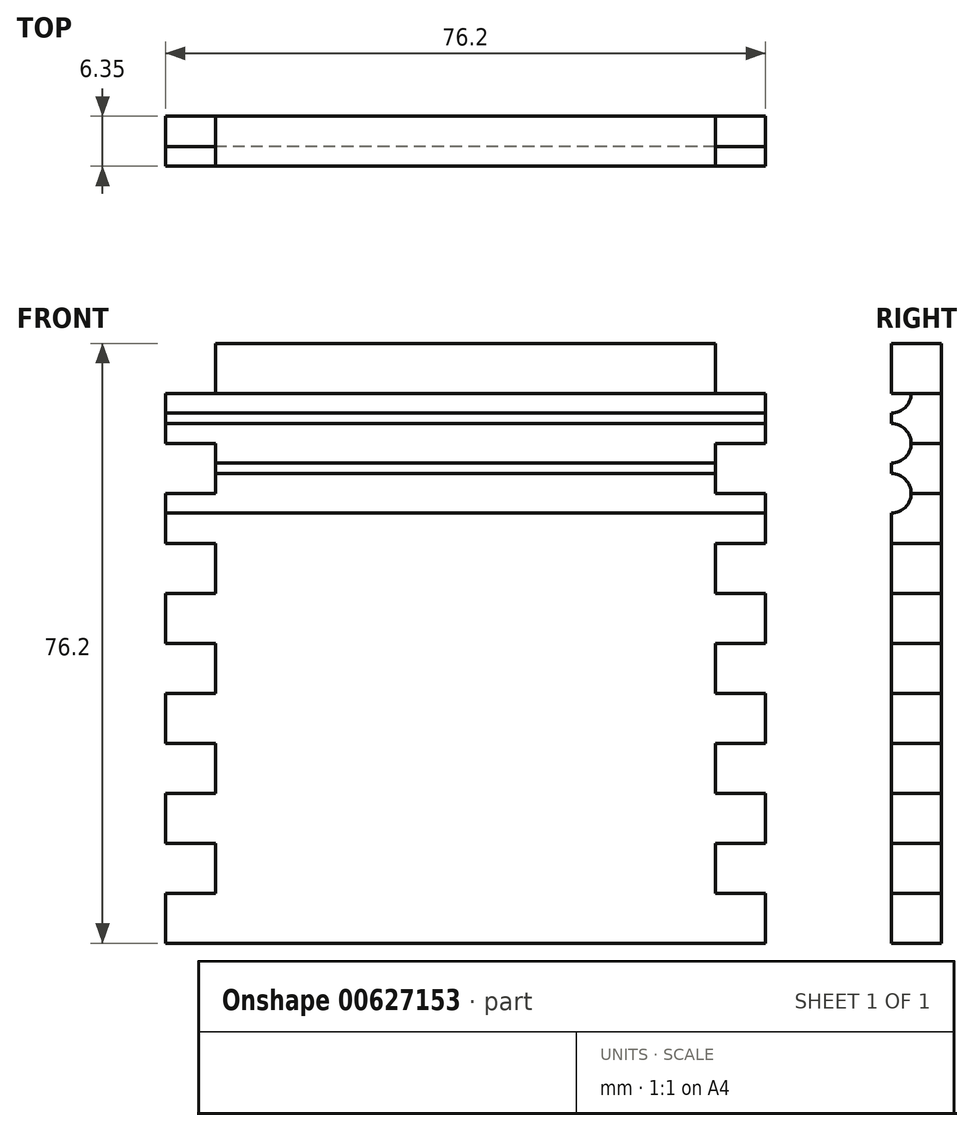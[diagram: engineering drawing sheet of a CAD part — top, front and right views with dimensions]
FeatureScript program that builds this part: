
annotation { "Feature Type Name" : "Feature", "Feature Type Description" : "" }
export const myFeature = defineFeature(function(context is Context, id is Id, definition is map)
    precondition{}
    {
        {
            var Q0;
            Q0=qCreatedBy(makeId("Front.planeOp"),FACE);
            var sketch = newSketch(context, id + "F0", { "sketchPlane" : qUnion([Q0])});
            skLineSegment(sketch, "E0", {"start": v(-134.03, 0) * mm, "end": v(134.03, 0) * mm, "construction": true});
            skLineSegment(sketch, "E1.bottom", {"start": v(-38.1, 38.1) * mm, "end": v(38.1, 38.1) * mm});
            skLineSegment(sketch, "E1.top", {"start": v(-38.1, -38.1) * mm, "end": v(38.1, -38.1) * mm});
            skLineSegment(sketch, "E1.left", {"start": v(-38.1, 38.1) * mm, "end": v(-38.1, -38.1) * mm});
            skLineSegment(sketch, "E1.right", {"start": v(38.1, 38.1) * mm, "end": v(38.1, -38.1) * mm});
            skLineSegment(sketch, "E2", {"start": v(0, 82.06) * mm, "end": v(0, -82.06) * mm, "construction": true});
            skLineSegment(sketch, "E3", {"start": v(-31.75, 38.1) * mm, "end": v(-31.75, -38.1) * mm, "construction": true});
            skLineSegment(sketch, "E4", {"start": v(31.75, 38.1) * mm, "end": v(31.75, -38.1) * mm, "construction": true});
            skLineSegment(sketch, "E5", {"start": v(-38.1, 31.75) * mm, "end": v(-31.75, 31.75) * mm});
            skLineSegment(sketch, "E6.0.1.0", {"start": v(-38.1, 25.4) * mm, "end": v(-31.75, 25.4) * mm});
            skLineSegment(sketch, "E6.0.2.0", {"start": v(-38.1, 19.05) * mm, "end": v(-31.75, 19.05) * mm});
            skLineSegment(sketch, "E6.0.3.0", {"start": v(-38.1, 12.7) * mm, "end": v(-31.75, 12.7) * mm});
            skLineSegment(sketch, "E6.0.4.0", {"start": v(-38.1, 6.35) * mm, "end": v(-31.75, 6.35) * mm});
            skLineSegment(sketch, "E6.0.5.0", {"start": v(-38.1, 0) * mm, "end": v(-31.75, 0) * mm});
            skLineSegment(sketch, "E6.0.6.0", {"start": v(-38.1, -6.35) * mm, "end": v(-31.75, -6.35) * mm});
            skLineSegment(sketch, "E6.0.7.0", {"start": v(-38.1, -12.7) * mm, "end": v(-31.75, -12.7) * mm});
            skLineSegment(sketch, "E6.0.8.0", {"start": v(-38.1, -19.05) * mm, "end": v(-31.75, -19.05) * mm});
            skLineSegment(sketch, "E6.0.9.0", {"start": v(-38.1, -25.4) * mm, "end": v(-31.75, -25.4) * mm});
            skLineSegment(sketch, "E6.0.10.0", {"start": v(-38.1, -31.75) * mm, "end": v(-31.75, -31.75) * mm});
            skLineSegment(sketch, "E6.0.11.0", {"start": v(-38.1, -38.1) * mm, "end": v(-31.75, -38.1) * mm});
            skLineSegment(sketch, "E6.direction1", {"start": v(-38.1, 31.75) * mm, "end": v(-13.1, 31.75) * mm, "construction": true});
            skLineSegment(sketch, "E6.direction2", {"start": v(-38.1, 31.75) * mm, "end": v(-38.1, 25.4) * mm, "construction": true});
            skLineSegment(sketch, "E7", {"start": v(-31.75, 38.1) * mm, "end": v(-31.75, 31.75) * mm});
            skLineSegment(sketch, "E8", {"start": v(-31.75, 25.4) * mm, "end": v(-31.75, 19.05) * mm});
            skLineSegment(sketch, "E9", {"start": v(-31.75, 12.7) * mm, "end": v(-31.75, 6.35) * mm});
            skLineSegment(sketch, "E10", {"start": v(-31.75, 0) * mm, "end": v(-31.75, -6.35) * mm});
            skLineSegment(sketch, "E11", {"start": v(-31.75, -12.7) * mm, "end": v(-31.75, -19.05) * mm});
            skLineSegment(sketch, "E12", {"start": v(-31.75, -25.4) * mm, "end": v(-31.75, -31.75) * mm});
            skLineSegment(sketch, "E13.MirrorCS", {"start": v(31.75, 38.1) * mm, "end": v(31.75, 31.75) * mm});
            skLineSegment(sketch, "E14.MirrorCS", {"start": v(38.1, 31.75) * mm, "end": v(38.1, 25.4) * mm, "construction": true});
            skLineSegment(sketch, "E15.MirrorCS", {"start": v(38.1, 31.75) * mm, "end": v(31.75, 31.75) * mm});
            skLineSegment(sketch, "E16.MirrorCS", {"start": v(38.1, 25.4) * mm, "end": v(31.75, 25.4) * mm});
            skLineSegment(sketch, "E17.MirrorCS", {"start": v(31.75, -25.4) * mm, "end": v(31.75, -31.75) * mm});
            skLineSegment(sketch, "E18.MirrorCS", {"start": v(31.75, 25.4) * mm, "end": v(31.75, 19.05) * mm});
            skLineSegment(sketch, "E19.MirrorCS", {"start": v(31.75, 12.7) * mm, "end": v(31.75, 6.35) * mm});
            skLineSegment(sketch, "E20.MirrorCS", {"start": v(31.75, -12.7) * mm, "end": v(31.75, -19.05) * mm});
            skLineSegment(sketch, "E21.MirrorCS", {"start": v(38.1, -38.1) * mm, "end": v(31.75, -38.1) * mm});
            skLineSegment(sketch, "E22.MirrorCS", {"start": v(31.75, 0) * mm, "end": v(31.75, -6.35) * mm});
            skLineSegment(sketch, "E23.MirrorCS", {"start": v(38.1, -25.4) * mm, "end": v(31.75, -25.4) * mm});
            skLineSegment(sketch, "E24.MirrorCS", {"start": v(38.1, -31.75) * mm, "end": v(31.75, -31.75) * mm});
            skLineSegment(sketch, "E25.MirrorCS", {"start": v(38.1, -19.05) * mm, "end": v(31.75, -19.05) * mm});
            skLineSegment(sketch, "E26.MirrorCS", {"start": v(38.1, 19.05) * mm, "end": v(31.75, 19.05) * mm});
            skLineSegment(sketch, "E27.MirrorCS", {"start": v(38.1, 12.7) * mm, "end": v(31.75, 12.7) * mm});
            skLineSegment(sketch, "E28.MirrorCS", {"start": v(38.1, 0) * mm, "end": v(31.75, 0) * mm});
            skLineSegment(sketch, "E29.MirrorCS", {"start": v(38.1, -6.35) * mm, "end": v(31.75, -6.35) * mm});
            skLineSegment(sketch, "E30.MirrorCS", {"start": v(38.1, -12.7) * mm, "end": v(31.75, -12.7) * mm});
            skLineSegment(sketch, "E31.MirrorCS", {"start": v(38.1, 6.35) * mm, "end": v(31.75, 6.35) * mm});
            skSolve(sketch);
        }
        {
            var Q0;
            Q0=makeQuery(id+"F0.imprint","IMPRINT",FACE,{"disambiguationData":[TD([[makeQuery(id+"F0.imprint","IMPRINT",EDGE,{"derivedFrom":sQuery(id+"F0.wireOp",EDGE,"E1.top")}),1.0]])]});
            extrude(context, id + "F1", {"entities" : qUnion([Q0]), "depth" : 6.35 * mm, "offsetDistance" : 25 * mm});
        }
        {
            var Q0;
            {var subQ0=sQuery(id+"F0.wireOp",EDGE,"E1.left");Q0=makeQuery(id+"F1.opExtrude","SWEPT_FACE",FACE,{"disambiguationData":[OSD([subQ0]),TDD([makeQuery(id+"F0.imprint","IMPRINT",EDGE,{"disambiguationData":[TD([[makeQuery(id+"F0.imprint","INTERSECT",VERTEX,{"derivedFrom":[subQ0,sQuery(id+"F0.wireOp",EDGE,"E5")]}),-1.0]])],"derivedFrom":subQ0})])]});}
            var sketch = newSketch(context, id + "F2", { "sketchPlane" : qUnion([Q0])});
            skLineSegment(sketch, "E32.0.0", {"start": v(0, 38.1) * mm, "end": v(0, 31.75) * mm, "construction": true});
            skLineSegment(sketch, "E32.0.1", {"start": v(0, 31.75) * mm, "end": v(6.35, 31.75) * mm, "construction": true});
            skLineSegment(sketch, "E32.0.2", {"start": v(6.35, 31.75) * mm, "end": v(6.35, 38.1) * mm, "construction": true});
            skLineSegment(sketch, "E32.0.3", {"start": v(6.35, 38.1) * mm, "end": v(0, 38.1) * mm, "construction": true});
            skLineSegment(sketch, "E33", {"start": v(6.35, 38.1) * mm, "end": v(6.35, 5.95) * mm, "construction": true});
            skLineSegment(sketch, "E34.0.0", {"start": v(0, 31.75) * mm, "end": v(0, 25.4) * mm, "construction": true});
            skLineSegment(sketch, "E34.0.1", {"start": v(0, 25.4) * mm, "end": v(6.35, 25.4) * mm, "construction": true});
            skLineSegment(sketch, "E34.0.2", {"start": v(6.35, 25.4) * mm, "end": v(6.35, 31.75) * mm, "construction": true});
            skLineSegment(sketch, "E34.0.3", {"start": v(6.35, 31.75) * mm, "end": v(0, 31.75) * mm, "construction": true});
            skLineSegment(sketch, "E35.0.0", {"start": v(0, 25.4) * mm, "end": v(0, 19.05) * mm, "construction": true});
            skLineSegment(sketch, "E35.0.1", {"start": v(0, 19.05) * mm, "end": v(6.35, 19.05) * mm, "construction": true});
            skLineSegment(sketch, "E35.0.2", {"start": v(6.35, 19.05) * mm, "end": v(6.35, 25.4) * mm, "construction": true});
            skLineSegment(sketch, "E35.0.3", {"start": v(6.35, 25.4) * mm, "end": v(0, 25.4) * mm, "construction": true});
            skLineSegment(sketch, "E36.0.0", {"start": v(0, 19.05) * mm, "end": v(0, 12.7) * mm, "construction": true});
            skLineSegment(sketch, "E36.0.1", {"start": v(0, 12.7) * mm, "end": v(6.35, 12.7) * mm, "construction": true});
            skLineSegment(sketch, "E36.0.2", {"start": v(6.35, 12.7) * mm, "end": v(6.35, 19.05) * mm, "construction": true});
            skLineSegment(sketch, "E36.0.3", {"start": v(6.35, 19.05) * mm, "end": v(0, 19.05) * mm, "construction": true});
            skCircle(sketch, "E37", {"center": v(6.35, 31.75) * mm, "radius": 2.5 * mm});
            skCircle(sketch, "E38", {"center": v(6.35, 25.4) * mm, "radius": 2.5 * mm});
            skCircle(sketch, "E39", {"center": v(6.35, 19.05) * mm, "radius": 2.5 * mm});
            skSolve(sketch);
        }
        {
            var Q0;
            {var subQ0=sQuery(id+"F2.wireOp",EDGE,"E37");var subQ1=sQuery(id+"F0.wireOp",EDGE,"E5");var subQ2=sQuery(id+"F0.wireOp",EDGE,"E1.left");var subQ3=makeQuery(id+"F1.opExtrude","SWEPT_EDGE",EDGE,{"disambiguationData":[OSD([subQ2,subQ1])]});var subQ4=makeQuery(id+"F2.imprint","INTERSECT",VERTEX,{"derivedFrom":[subQ3,subQ0]});Q0=makeQuery(id+"F2.imprint","IMPRINT",FACE,{"disambiguationData":[TD([[makeQuery(id+"F2.imprint","IMPRINT",EDGE,{"disambiguationData":[TD([[subQ4,-1.0]])],"derivedFrom":subQ0}),1.0]])]});}
            var Q1;
            {var subQ0=sQuery(id+"F2.wireOp",EDGE,"E38");var subQ1=sQuery(id+"F0.wireOp",EDGE,"E6.0.1.0");var subQ2=sQuery(id+"F0.wireOp",EDGE,"E1.left");var subQ3=makeQuery(id+"F1.opExtrude","SWEPT_EDGE",EDGE,{"disambiguationData":[OSD([subQ2,subQ1])]});var subQ4=makeQuery(id+"F2.imprint","INTERSECT",VERTEX,{"derivedFrom":[subQ3,subQ0]});Q1=makeQuery(id+"F2.imprint","IMPRINT",FACE,{"disambiguationData":[TD([[makeQuery(id+"F2.imprint","IMPRINT",EDGE,{"disambiguationData":[TD([[subQ4,1.0]])],"derivedFrom":subQ0}),1.0]])]});}
            var Q2;
            {var subQ0=sQuery(id+"F2.wireOp",EDGE,"E38");var subQ1=sQuery(id+"F0.wireOp",EDGE,"E6.0.1.0");var subQ2=sQuery(id+"F0.wireOp",EDGE,"E1.left");var subQ3=makeQuery(id+"F1.opExtrude","SWEPT_EDGE",EDGE,{"disambiguationData":[OSD([subQ2,subQ1])]});var subQ4=makeQuery(id+"F2.imprint","INTERSECT",VERTEX,{"derivedFrom":[subQ3,subQ0]});Q2=makeQuery(id+"F2.imprint","IMPRINT",FACE,{"disambiguationData":[TD([[makeQuery(id+"F2.imprint","IMPRINT",EDGE,{"disambiguationData":[TD([[subQ4,-1.0]])],"derivedFrom":subQ0}),1.0]])]});}
            var Q3;
            Q3=makeQuery(id+"F2.imprint","IMPRINT",FACE,{"disambiguationData":[TD([[makeQuery(id+"F2.imprint","IMPRINT",EDGE,{"derivedFrom":sQuery(id+"F2.wireOp",EDGE,"E39")}),1.0]])]});
            extrude(context, id + "F3", {"entities" : qUnion([Q0, Q1, Q2, Q3]), "operationType" : NewBodyOperationType.REMOVE, "endBound" : BoundingType.THROUGH_ALL, "oppositeDirection" : true, "depth" : 25 * mm, "offsetDistance" : 25 * mm});
        }
    });
